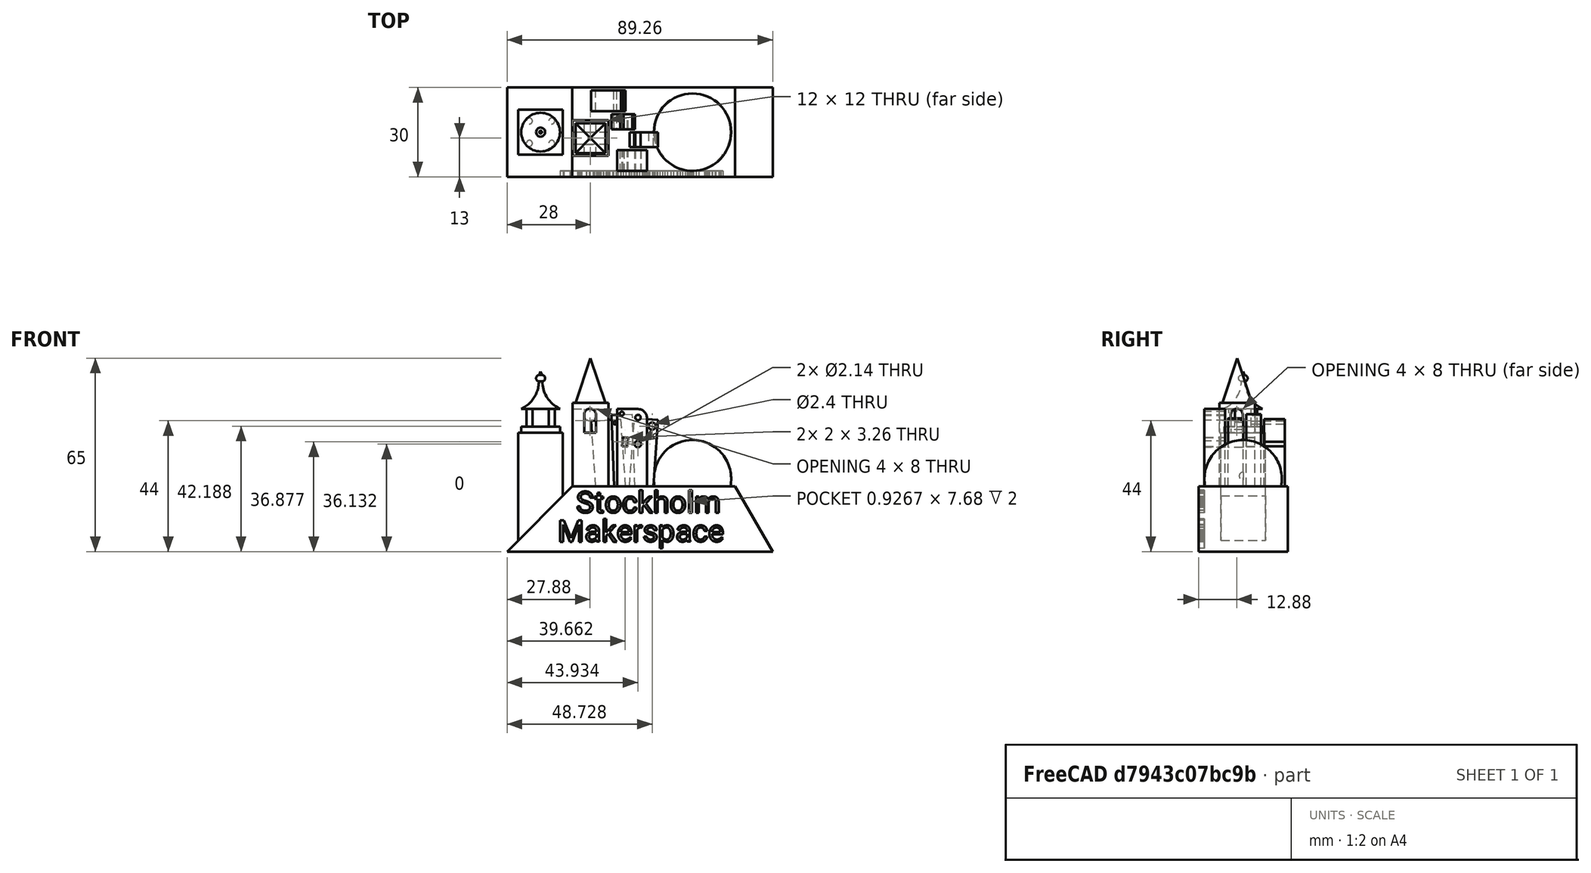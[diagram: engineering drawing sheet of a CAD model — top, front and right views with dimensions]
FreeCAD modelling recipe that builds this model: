
FCSTD DOCUMENT  (FreeCAD 0.17RUnknown)
Label: makerstand
License: All rights reserved
LicenseURL: http://en.wikipedia.org/wiki/All_rights_reserved
objects: PartDesign::AdditiveBox×6, Sketcher::SketchObject×5, PartDesign::Pocket×3, Part::Part2DObjectPython×2, Part::Extrusion×2, PartDesign::AdditiveCylinder×2, PartDesign::LinearPattern×2, PartDesign::Pad×1, PartDesign::AdditiveSphere×1, PartDesign::MultiTransform×1, PartDesign::Revolution×1, PartDesign::AdditiveWedge×1, PartDesign::Fillet×1, PartDesign::Body×1, Part::MultiFuse×1, Part::Cut×1, Mesh::Feature×1
note: 46 computed .brp shape members not serialized (recipe doc carries the construction recipe); baked Part::Feature solids carry a one-line shape summary decoded from their .brp

FEATURE [Sketcher::SketchObject] Sketch  label="Base_plate"
  MapMode = 5
  Placement = pos=(0,0,0) rot=(1,0,0;1.5708rad)
  Support = -> [XZ_Plane]
  expr: Constraints[9] = Extrude_Makerspace.Shape.BoundBox.XLength
  sketch-geometry (4):
    g0: LineSegment StartX=0 StartY=0 StartZ=0 EndX=21.92 EndY=21.92 EndZ=0
    g1: LineSegment StartX=21.92 StartY=21.92 StartZ=0 EndX=76.6067 EndY=21.92 EndZ=0
    g2: LineSegment StartX=76.6067 StartY=21.92 StartZ=0 EndX=89.2622 EndY=0 EndZ=0
    g3: LineSegment StartX=89.2622 StartY=0 StartZ=0 EndX=0 EndY=0 EndZ=0
  constraints (11):
    c: Coincident(g-1,g0)
    c: Coincident(g0,g1)
    c: Horizontal(g1)
    c: Coincident(g1,g2)
    c: PointOnObject(g2,g-1)
    c: Coincident(g2,g3)
    c: Coincident(g3,g0)
    c: Angle(g3,g0) = 0.785398
    c: Angle(g2,g3) = 1.0472
    c: Distance(g1) = 54.6867
    c: DistanceY(g-1,g0) = 21.92
FEATURE [PartDesign::Pad] Pad
  Length = 30
  Length2 = 100
  Midplane = true
  Placement = pos=(0,0,0) rot=(1,0,0;1.5708rad)
  Profile = -> Sketch
  Type = 0
FEATURE [Part::Part2DObjectPython] ShapeString  label="String_Stockholm"  # Draft 2D object (typed FeaturePython)
  FontFile = <userpath>/.bin/idea-IC-182.5107.16/plugins/android/lib/layoutlib/data/fonts/DroidSans.ttf
  Placement = pos=(23.17,-15,13) rot=(1,0,0;1.5708rad)
  Size = 8
  String = Stockholm
  Tracking = 0
FEATURE [Part::Part2DObjectPython] ShapeString001  label="String_Makerspace"  # Draft 2D object (typed FeaturePython)
  FontFile = <userpath>/.bin/idea-IC-182.5107.16/plugins/android/lib/layoutlib/data/fonts/DroidSans.ttf
  Placement = pos=(17,-15,3.3) rot=(1,0,0;1.5708rad)
  Size = 8
  String = Makerspace
  Tracking = 0
  expr: Placement.Base.y = String_Stockholm.Placement.Base.y
FEATURE [Part::Extrusion] Extrude  label="Extrude_Stockholm"
  Base = -> ShapeString
  Dir = (0,-1,0)
  DirMode = 2
  FaceMakerClass = Part::FaceMakerBullseye
  LengthFwd = 1
  LengthRev = 2
  Solid = false
  Symmetric = false
FEATURE [Part::Extrusion] Extrude001  label="Extrude_Makerspace"
  Base = -> ShapeString001
  Dir = (0,-1,0)
  DirMode = 2
  FaceMakerClass = Part::FaceMakerBullseye
  LengthFwd = 1
  LengthRev = 2
  Solid = false
  Symmetric = false
FEATURE [PartDesign::AdditiveSphere] Sphere
  Angle1 = -90
  Angle2 = 90
  Angle3 = 360
  AttacherType = Attacher::AttachEngine3D
  AttachmentOffset = pos=(-14.3,-15,2.6) rot=(0,0,1;0rad)
  BaseFeature = -> Pad
  MapMode = 1
  Placement = pos=(62.3067,0,24.52) rot=(0,0,1;0rad)
  Radius = 13
  Support = -> [Pad]
  expr: AttachmentOffset.Base.z = Radius / 5
  expr: AttachmentOffset.Base.x = -Radius * 1.1000000000000001
  expr: AttachmentOffset.Base.y = -Pad.Length / 2
FEATURE [PartDesign::AdditiveBox] Box  label="StadshusBas"
  AttacherType = Attacher::AttachEngine3D
  AttachmentOffset = pos=(3.75,-7.5,0) rot=(0,0,1;0rad)
  BaseFeature = -> Sphere
  Height = 40
  Length = 15
  MapMode = 2
  Placement = pos=(3.75,-7.5,0) rot=(0,0,1;0rad)
  Support = -> [X_Axis]
  Width = 15
  expr: AttachmentOffset.Base.x = Length / 4
  expr: AttachmentOffset.Base.y = -Length / 2
FEATURE [PartDesign::AdditiveCylinder] Cylinder  label="Stadshus_pillar"
  Angle = 360
  AttacherType = Attacher::AttachEngine3D
  AttachmentOffset = pos=(3.75,3.75,0) rot=(0,0,1;0rad)
  BaseFeature = -> Box
  Height = 8
  MapMode = 1
  Placement = pos=(7.5,-3.75,40) rot=(0,0,1;0rad)
  Radius = 1
  Support = -> [Box]
  expr: AttachmentOffset.Base.y = StadshusBas001.Width / 4
  expr: AttachmentOffset.Base.x = StadshusBas001.Length / 4
FEATURE [PartDesign::LinearPattern] LinearPattern
  Direction = -> X_Axis
  Length = 7.5
  Occurrences = 2
  Placement = pos=(7.5,-3.75,40) rot=(0,0,1;0rad)
  expr: Length = StadshusBas.Length / 2
FEATURE [PartDesign::LinearPattern] LinearPattern001
  Direction = -> Y_Axis
  Length = 7.5
  Occurrences = 2
  Placement = pos=(7.5,-3.75,40) rot=(0,0,1;0rad)
  expr: Length = StadshusBas.Length / 2
FEATURE [PartDesign::MultiTransform] MultiTransform
  BaseFeature = -> Cylinder
  Originals = -> [Cylinder]
  Placement = pos=(7.5,-3.75,40) rot=(0,0,1;0rad)
  Transformations = -> [LinearPattern,LinearPattern001]
FEATURE [PartDesign::AdditiveCylinder] Cylinder001  label="Stadshused_battlement"
  Angle = 360
  AttacherType = Attacher::AttachEngine3D
  BaseFeature = -> MultiTransform
  Height = 2
  MapMode = 45
  Placement = pos=(11.25,0,40) rot=(0,0,1;0rad)
  Radius = 6.5
  Support = -> [MultiTransform]
FEATURE [Sketcher::SketchObject] Sketch001
  AttachmentOffset = pos=(11.25,48,0) rot=(0,0,1;0rad)
  MapMode = 5
  Placement = pos=(11.25,-5e-12,48) rot=(1,0,0;1.5708rad)
  Support = -> [XZ_Plane]
  expr: AttachmentOffset.Base.x = StadshusBas001.Length / 4 - StadshusBas001.Placement.Base.y
  expr: AttachmentOffset.Base.z = StadshusBas001.Placement.Base.x - StadshusBas001.Length / 4
  expr: AttachmentOffset.Base.y = StadshusBas001.Height + Stadshus_pillar.Height
  expr: Constraints.base = Stadshused_battlement.Radius
  expr: Constraints[12] = Constraints.base / 5
  expr: Constraints[18] = Constraints.base / 6
  sketch-geometry (9):
    g0: LineSegment StartX=0 StartY=0 StartZ=0 EndX=6.5 EndY=0 EndZ=0
    g1: LineSegment StartX=6.5 StartY=0 StartZ=0 EndX=5.63397 EndY=0.5 EndZ=0
    g2: ArcOfCircle CenterX=10.6679 CenterY=9.21908 CenterZ=0 NormalX=0 NormalY=0 NormalZ=1 AngleXU=0 Radius=10.0679 StartAngle=3.14159 EndAngle=4.18879
    g3: ArcOfCircle CenterX=0.444626 CenterY=10.2912 CenterZ=0 NormalX=0 NormalY=0 NormalZ=1 AngleXU=0 Radius=1.08333 StartAngle=4.85631 EndAngle=7.85398
    g4: GeomPoint X=0.444626 Y=11.3745 Z=0
    g5: LineSegment StartX=0 StartY=12.5961 StartZ=0 EndX=0.444626 EndY=11.3745 EndZ=0
    g6: LineSegment StartX=0 StartY=12.5961 StartZ=0 EndX=0 EndY=0 EndZ=0
    g7: LineSegment [constr] StartX=0.444626 StartY=11.3745 StartZ=0 EndX=0 EndY=11.3745 EndZ=0
    g8: LineSegment [constr] StartX=0.6 StartY=9.21908 StartZ=0 EndX=0 EndY=9.21908 EndZ=0
  constraints (26):
    c: Coincident(g-1,g0)
    c: Horizontal(g0)
    c: Coincident(g2,g1)
    c: Tangent(g2,g1)
    c: Distance(g1) = 1
    c: Coincident(g4,g3)
    c: Coincident(g5,g3)
    c: PointOnObject(g5,g-2)
    c: Angle(g-2,g5) = 0.349066
    c: Coincident(g6,g5)
    c: Coincident(g6,g-1)
    c: Distance(g0) = 6.5  'base'
    c: Distance(g5) = 1.3
    c: Coincident(g7,g3)
    c: PointOnObject(g7,g6)
    c: Horizontal(g7)
    c: Tangent(g7,g3)
    c: Coincident(g2,g3)
    c: Radius(g3) = 1.08333
    c: Coincident(g8,g2)
    c: PointOnObject(g8,g6)
    c: Horizontal(g8)
    c: Distance(g8) = 0.6
    c: Coincident(g1,g0)
    c: DistanceY(g-1,g1) = 0.5
    c: Perpendicular(g2,g8)
FEATURE [PartDesign::Revolution] Revolution
  Angle = 360
  Axis = (0,0,1)
  Base = (11.25,0,48)
  BaseFeature = -> Cylinder001
  Placement = pos=(11.25,0,40) rot=(0,0,1;0rad)
  Profile = -> Sketch001
  ReferenceAxis = -> Sketch001 [V_Axis]
  Reversed = true
FEATURE [PartDesign::AdditiveBox] Box001  label="Olof_bas"
  AttacherType = Attacher::AttachEngine3D
  AttachmentOffset = pos=(22,-8,0) rot=(0,0,1;0rad)
  BaseFeature = -> Revolution
  Height = 50
  Length = 12
  MapMode = 2
  Placement = pos=(22,-8,0) rot=(0,0,1;0rad)
  Support = -> [X_Axis]
  Width = 12
  expr: AttachmentOffset.Base.y = -Width / 1.5
FEATURE [PartDesign::AdditiveWedge] Wedge
  AttacherType = Attacher::AttachEngine3D
  AttachmentOffset = pos=(1,1,0) rot=(0.57735,0.57735,0.57735;2.0944rad)
  BaseFeature = -> Box001
  MapMode = 5
  Placement = pos=(23,-7,50) rot=(0.57735,0.57735,0.57735;2.0944rad)
  Support = -> [Box001]
  X2max = 5
  X2min = 5
  Xmax = 10
  Xmin = 0
  Ymax = 15
  Ymin = 0
  Z2max = 5
  Z2min = 5
  Zmax = 10
  Zmin = 0
  expr: AttachmentOffset.Base.y = Olof_bas.Width / 2 - Xmax / 2
  expr: AttachmentOffset.Base.x = Olof_bas.Width / 2 - Xmax / 2
FEATURE [Sketcher::SketchObject] Sketch002  label="olof_window1"
  ExternalGeometry = -> [Wedge]
  MapMode = 5
  Placement = pos=(23,-8,50) rot=(0.57735,0.57735,-0.57735;2.0944rad)
  Support = -> [Wedge]
  expr: Constraints.top_margin = 4
  sketch-geometry (4):
    g0: LineSegment StartX=3.99999 StartY=6.88 StartZ=0 EndX=9.99999 EndY=6.88 EndZ=0
    g1: LineSegment StartX=9.99999 StartY=6.88 StartZ=0 EndX=9.99999 EndY=2.88 EndZ=0
    g2: LineSegment StartX=9.99999 StartY=2.88 StartZ=0 EndX=4.00001 EndY=2.88 EndZ=0
    g3: ArcOfCircle CenterX=4 CenterY=4.88 CenterZ=0 NormalX=0 NormalY=0 NormalZ=1 AngleXU=0 Radius=2 StartAngle=1.5708 EndAngle=4.7124
  constraints (13):
    c: Coincident(g0,g1)
    c: Coincident(g1,g2)
    c: Horizontal(g0)
    c: Horizontal(g2)
    c: Vertical(g1)
    c: Coincident(g3,g2)
    c: Coincident(g3,g0)
    c: Distance(g1) = 4  'window_width'
    c: Distance(g0) = 6  'window_height'
    c: Angle(g3) = 3.14159
    c: Tangent(g3,g2)
    c: DistanceX(g-3,g3) = 4  'top_margin'
    c: DistanceY(g-3,g3) = 5.88  'side_margin'
FEATURE [PartDesign::Pocket] Pocket
  BaseFeature = -> Wedge
  Length = 5
  Length2 = 100
  Placement = pos=(23,-7,50) rot=(0.57735,0.57735,0.57735;2.0944rad)
  Profile = -> Sketch002
  Type = 2
FEATURE [Sketcher::SketchObject] Sketch003
  ExternalGeometry = -> [Pocket]
  MapMode = 5
  Placement = pos=(34,-7,50) rot=(0.57735,0.57735,0.57735;2.0944rad)
  Support = -> [Pocket]
  expr: Constraints[10] = olof_window1.Constraints.side_margin
  expr: Constraints[9] = olof_window1.Constraints.top_margin
  expr: Constraints[8] = olof_window1.Constraints.window_height
  expr: Constraints[7] = olof_window1.Constraints.window_width
  sketch-geometry (4):
    g0: ArcOfCircle CenterX=4.88 CenterY=-4 CenterZ=0 NormalX=0 NormalY=0 NormalZ=1 AngleXU=0 Radius=2 StartAngle=0 EndAngle=3.14159
    g1: LineSegment StartX=2.88 StartY=-4 StartZ=0 EndX=2.88 EndY=-10 EndZ=0
    g2: LineSegment StartX=6.88 StartY=-4 StartZ=0 EndX=6.88 EndY=-10 EndZ=0
    g3: LineSegment StartX=2.88 StartY=-10 StartZ=0 EndX=6.88 EndY=-10 EndZ=0
  constraints (11):
    c: Tangent(g0,g2) = 1.5708
    c: Tangent(g0,g1) = -1.5708
    c: Vertical(g1)
    c: Coincident(g3,g1)
    c: Coincident(g3,g2)
    c: Horizontal(g3)
    c: Vertical(g2)
    c: Distance(g3) = 4
    c: DistanceY(g2,g2) = 6
    c: DistanceY(g0,g-3) = 4
    c: DistanceX(g-3,g0) = 5.88
FEATURE [PartDesign::Pocket] Pocket001
  BaseFeature = -> Pocket
  Length = 0
  Length2 = 100
  Placement = pos=(23,-7,50) rot=(0.57735,0.57735,0.57735;2.0944rad)
  Profile = -> Sketch003
  Type = 3
  UpToFace = -> Pocket [Face12]
FEATURE [PartDesign::AdditiveBox] Box002
  AttacherType = Attacher::AttachEngine3D
  AttachmentOffset = pos=(-21,7,-3) rot=(1,0,0;0.069813rad)
  BaseFeature = -> Pocket001
  Height = 25
  Length = 7
  MapMode = 5
  Placement = pos=(30,14,18.92) rot=(0.034878,-0.034878,-0.998783;1.57201rad)
  Support = -> [Pocket001]
  Width = 10
FEATURE [PartDesign::AdditiveBox] Box003
  AttacherType = Attacher::AttachEngine3D
  AttachmentOffset = pos=(8,6,-2) rot=(1,0,0;0.034907rad)
  BaseFeature = -> Box002
  Height = 26
  Length = 5
  MapMode = 5
  Placement = pos=(36,6,19.92) rot=(0.01745,-0.01745,-0.999695;1.5711rad)
  Support = -> [Box002]
  Width = 7
FEATURE [PartDesign::AdditiveBox] Box004
  AttacherType = Attacher::AttachEngine3D
  AttachmentOffset = pos=(12,1,-1) rot=(0,0,1;0rad)
  BaseFeature = -> Box003
  Height = 27
  Length = 7
  MapMode = 5
  Placement = pos=(37,-6,20.92) rot=(0,0,-1;1.5708rad)
  Support = -> [Box003]
  Width = 10
FEATURE [PartDesign::AdditiveBox] Box005
  AttacherType = Attacher::AttachEngine3D
  AttachmentOffset = pos=(-6,4,-2) rot=(-1,0,0;0.069813rad)
  BaseFeature = -> Box004
  Height = 25
  Length = 5
  MapMode = 5
  Placement = pos=(41,-5e-12,19.92) rot=(-0.034878,0.034878,-0.998783;1.57201rad)
  Support = -> [Box004]
  Width = 8
FEATURE [PartDesign::Fillet] Fillet
  Base = -> Box005 [Edge91]
  BaseFeature = -> Box005
  Placement = pos=(41,-5e-12,19.92) rot=(-0.034878,0.034878,-0.998783;1.57201rad)
  Radius = 3
FEATURE [Sketcher::SketchObject] Sketch004
  MapMode = 5
  Placement = pos=(41,-15,19.92) rot=(0.998783,0.034878,-0.034878;1.57201rad)
  Support = -> [Fillet]
  sketch-geometry (9):
    g0: Circle CenterX=1.23323 CenterY=25.3318 CenterZ=0 NormalX=0 NormalY=0 NormalZ=1 AngleXU=0 Radius=0.9
    g1: Circle CenterX=-4.29911 CenterY=26.2226 CenterZ=0 NormalX=0 NormalY=0 NormalZ=1 AngleXU=0 Radius=0.67
    g2: Circle CenterX=1.79584 CenterY=16.3769 CenterZ=0 NormalX=0 NormalY=0 NormalZ=1 AngleXU=0 Radius=1.07
    g3: Circle CenterX=6.15607 CenterY=22.7532 CenterZ=0 NormalX=0 NormalY=0 NormalZ=1 AngleXU=0 Radius=1.2
    g4: Circle CenterX=-6.36202 CenterY=22.9407 CenterZ=0 NormalX=0 NormalY=0 NormalZ=1 AngleXU=0 Radius=0.53
    g5: LineSegment StartX=-3.40831 StartY=15.2517 StartZ=0 EndX=-1.62671 EndY=15.2517 EndZ=0
    g6: LineSegment StartX=-1.62671 StartY=15.2517 StartZ=0 EndX=-1.62671 EndY=18.393 EndZ=0
    g7: LineSegment StartX=-1.62671 StartY=18.393 StartZ=0 EndX=-3.40831 EndY=18.393 EndZ=0
    g8: LineSegment StartX=-3.40831 StartY=18.393 StartZ=0 EndX=-3.40831 EndY=15.2517 EndZ=0
  constraints (27):
    c: DistanceX(g4) = -6.36202
    c: DistanceY(g4) = 22.9407
    c: DistanceX(g1) = -4.29911
    c: DistanceY(g1) = 26.2226
    c: DistanceX(g0) = 1.23323
    c: DistanceY(g0) = 25.3318
    c: DistanceX(g3) = 6.15607
    c: DistanceY(g3) = 22.7532
    c: DistanceX(g2) = 1.79584
    c: DistanceY(g2) = 16.3769
    c: Radius(g4) = 0.53
    c: Radius(g1) = 0.67
    c: Radius(g0) = 0.9
    c: Radius(g3) = 1.2
    c: Radius(g2) = 1.07
    c: Coincident(g5,g6)
    c: Coincident(g6,g7)
    c: Coincident(g7,g8)
    c: Coincident(g8,g5)
    c: Horizontal(g5)
    c: Horizontal(g7)
    c: Vertical(g6)
    c: Vertical(g8)
    c: DistanceX(g5) = -3.40831
    c: DistanceY(g5) = 15.2517
    c: DistanceX(g6) = -1.62671
    c: DistanceY(g6) = 18.393
FEATURE [PartDesign::Pocket] Pocket002
  BaseFeature = -> Fillet
  Length = 5
  Length2 = 100
  Placement = pos=(41,-5e-12,19.92) rot=(-0.034878,0.034878,-0.998783;1.57201rad)
  Profile = -> Sketch004
  Type = 1
FEATURE [PartDesign::Body] Body
  Group = -> [Sketch,Pad,Sphere,Box,Cylinder,MultiTransform,LinearPattern,LinearPattern001,Cylinder001,Sketch001,Revolution,Box001,Wedge,Sketch002,Pocket,Sketch003,Pocket001,Box002,Box003,Box004,Box005,Fillet,Sketch004,Pocket002]
  Origin = -> Origin
  Tip = -> Pocket002
FEATURE [Part::MultiFuse] Fusion
  Shapes = -> [Extrude,Extrude001]
FEATURE [Part::Cut] Cut
  Base = -> Body
  Tool = -> Fusion
FEATURE [Mesh::Feature] Mesh  label="Cut (Meshed)"
